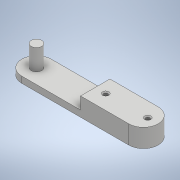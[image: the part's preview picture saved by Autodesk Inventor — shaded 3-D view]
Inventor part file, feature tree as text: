
AUTODESK INVENTOR PART (.ipt)
format: ipt  version: 2020 (Build 240168000, 168)  size: 126,976 bytes
history: native  units: mm
features: sketch x4, extrude x3, other x1, hole x1, projected_geometry x1
ambient origin geometry x8: Origin, YZ Plane, XZ Plane, XY Plane, X Axis, Y Axis, Z Axis, Center Point
bodies: Body1 (feature_tree)
feature tree (10):
  other  "Твердое тело1"
  extrude  "Выдавливание1"  Depth=25.5mm
  extrude  "Выдавливание2"  Depth=7.0mm
  extrude  "Выдавливание4"  Depth=1.5mm TaperAngle=0.0deg
  hole  "Отверстие1"  [1 undecoded]
  sketch  "Эскиз1"
  sketch  "Эскиз2"
  sketch  "Эскиз4"
  projected_geometry  "Спроецированная петля1"
  sketch  "Эскиз5"
note: 1 required parameter value undecoded (feature->parameter linkage not recoverable at this tier; creation-order binding heuristic only, values carry confidence <= 0.55)
